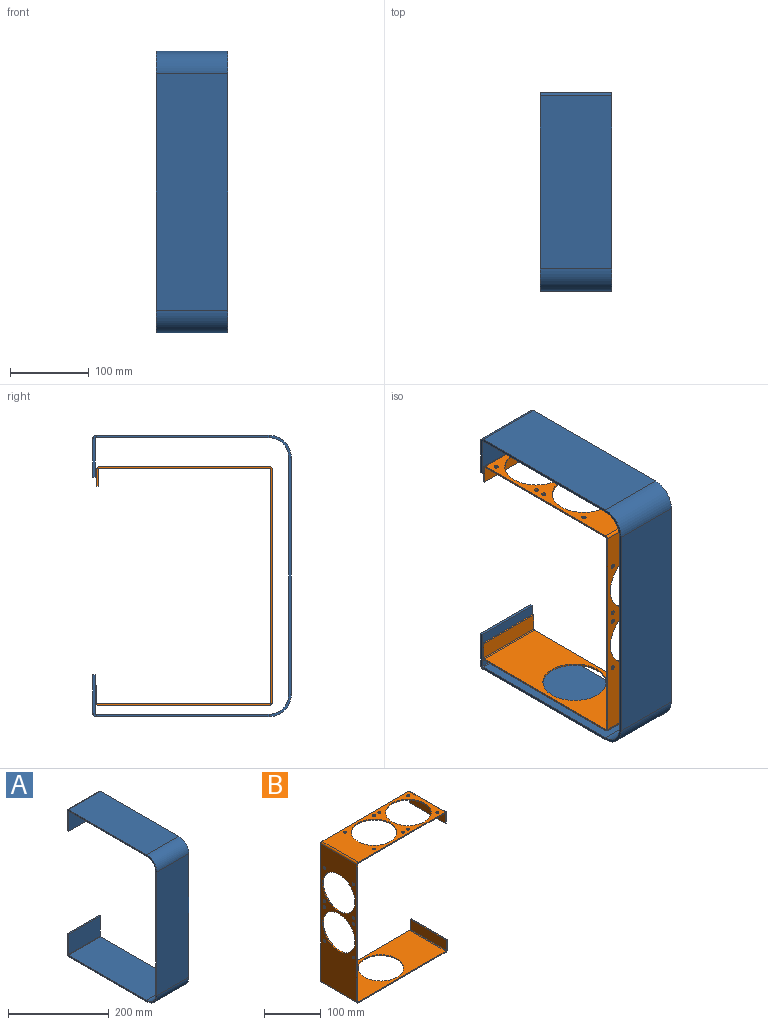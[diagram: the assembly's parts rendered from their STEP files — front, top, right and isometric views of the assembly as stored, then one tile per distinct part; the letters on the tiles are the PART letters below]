
ASSEMBLY  parts=2 mates=1
PART A: 38 faces, bbox 90x251.5x356.5 mm
  f0: plane 48.98x3.26mm, normal (-1,0,0), area 159.7mm2, adj f2,f3,f4,f18
  f1: plane 48.98x3.26mm, normal (1,0,0), area 159.7mm2, adj f2,f3,f4,f17
  f2: plane 90x3.26mm, normal (0,0,-1), area 293.4mm2, adj f0,f1,f3,f4
  f3: plane 90x48.98mm, normal (0,1,0), area 4408.6mm2, adj f0,f1,f2,f19
  f4: plane 90x48.98mm, normal (0,-1,0), area 4408.6mm2, adj f0,f1,f2,f20
  f5: plane 300x3.26mm, normal (-1,0,0), area 978mm2, adj f7,f8,f13,f34
  f6: plane 300x3.26mm, normal (1,0,0), area 978mm2, adj f7,f8,f14,f35
  f7: plane 300x90mm, normal (0,-1,0), area 27000mm2, adj f5,f6,f15,f36
  f8: plane 300x90mm, normal (0,1,0), area 27000mm2, adj f5,f6,f16,f37
  f9: plane 218.98x3.26mm, normal (-1,0,0), area 713.9mm2, adj f11,f12,f13,f18
  f10: plane 218.98x3.26mm, normal (1,0,0), area 713.9mm2, adj f11,f12,f14,f17
  f11: plane 218.98x90mm, normal (0,0,1), area 19708.6mm2, adj f9,f10,f15,f19
  f12: plane 218.98x90mm, normal (0,0,-1), area 19708.6mm2, adj f9,f10,f16,f20
  f13: plane 28.26x28.26mm, normal (-1,0,0), area 136.4mm2, adj f5,f9,f15,f16
  f14: plane 28.26x28.26mm, normal (1,0,0), area 136.4mm2, adj f6,f10,f15,f16
  f15: cylinder r=28.26mm len=90mm, axis (1,0,0), area 3995.2mm2, adj f7,f11,f13,f14
  f16: cylinder r=25mm len=90mm, axis (1,0,0), area 3534.3mm2, adj f8,f12,f13,f14
  f17: plane 4.28x4.28mm, normal (1,0,0), area 13.5mm2, adj f1,f10,f19,f20
  f18: plane 4.28x4.28mm, normal (-1,0,0), area 13.5mm2, adj f0,f9,f19,f20
  f19: cylinder r=4.28mm len=90mm, axis (1,0,0), area 604.5mm2, adj f3,f11,f17,f18
  f20: cylinder r=1.02mm len=90mm, axis (1,0,0), area 143.6mm2, adj f4,f12,f17,f18
  f21: plane 218.98x3.26mm, normal (-1,0,0), area 713.9mm2, adj f23,f24,f31,f34
  f22: plane 218.98x3.26mm, normal (1,0,0), area 713.9mm2, adj f23,f24,f30,f35
  f23: plane 218.98x90mm, normal (0,0,-1), area 19708.6mm2, adj f21,f22,f32,f36
  f24: plane 218.98x90mm, normal (0,0,1), area 19708.6mm2, adj f21,f22,f33,f37
  f25: plane 48.98x3.26mm, normal (-1,0,0), area 159.7mm2, adj f26,f28,f29,f31
  f26: plane 90x3.26mm, normal (0,0,1), area 293.4mm2, adj f25,f27,f28,f29
  f27: plane 48.98x3.26mm, normal (1,0,0), area 159.7mm2, adj f26,f28,f29,f30
  f28: plane 90x48.98mm, normal (0,1,0), area 4408.6mm2, adj f25,f26,f27,f32
  f29: plane 90x48.98mm, normal (0,-1,0), area 4408.6mm2, adj f25,f26,f27,f33
  f30: plane 4.28x4.28mm, normal (1,0,0), area 13.5mm2, adj f22,f27,f32,f33
  f31: plane 4.28x4.28mm, normal (-1,0,0), area 13.5mm2, adj f21,f25,f32,f33
  f32: cylinder r=4.28mm len=90mm, axis (1,0,0), area 604.5mm2, adj f23,f28,f30,f31
  f33: cylinder r=1.02mm len=90mm, axis (1,0,0), area 143.6mm2, adj f24,f29,f30,f31
  f34: plane 28.26x28.26mm, normal (-1,0,0), area 136.4mm2, adj f5,f21,f36,f37
  f35: plane 28.26x28.26mm, normal (1,0,0), area 136.4mm2, adj f6,f22,f36,f37
  f36: cylinder r=28.26mm len=90mm, axis (1,0,0), area 3995.2mm2, adj f7,f23,f34,f35
  f37: cylinder r=25mm len=90mm, axis (1,0,0), area 3534.3mm2, adj f8,f24,f34,f35
PART B: 59 faces, bbox 224.1x90x302.1 mm
  f0: plane 217.97x2.06mm, normal (0,-1,0), area 449mm2, adj f3,f4,f46,f55
  f1: plane 217.97x2.06mm, normal (0,1,0), area 449mm2, adj f3,f4,f47,f56
  f2: cylinder r=40mm len=80mm, axis (0,0,1), area 517.7mm2, adj f3,f4
  f3: plane 217.97x90mm, normal (0,0,-1), area 14590.6mm2, adj f0,f1,f2,f48,f57
  f4: plane 217.97x90mm, normal (0,0,1), area 14590.6mm2, adj f0,f1,f2,f49,f58
  f5: plane 295.91x2.06mm, normal (0,1,0), area 609.6mm2, adj f17,f18,f43,f47
  f6: cylinder r=2.75mm len=5.5mm, axis (-1,0,0), area 35.6mm2, adj f17,f18
  f7: cylinder r=2.75mm len=5.5mm, axis (-1,0,0), area 35.6mm2, adj f17,f18
  f8: cylinder r=2.75mm len=5.5mm, axis (-1,0,0), area 35.6mm2, adj f17,f18
  f9: cylinder r=2.75mm len=5.5mm, axis (-1,0,0), area 35.6mm2, adj f17,f18
  f10: cylinder r=2.75mm len=5.5mm, axis (-1,0,0), area 35.6mm2, adj f17,f18
  f11: cylinder r=2.75mm len=5.5mm, axis (-1,0,0), area 35.6mm2, adj f17,f18
  f12: cylinder r=2.75mm len=5.5mm, axis (-1,0,0), area 35.6mm2, adj f17,f18
  f13: cylinder r=2.75mm len=5.5mm, axis (-1,0,0), area 35.6mm2, adj f17,f18
  f14: cylinder r=40mm len=80mm, axis (-1,0,0), area 517.7mm2, adj f17,f18
  f15: cylinder r=40mm len=80mm, axis (-1,0,0), area 517.7mm2, adj f17,f18
  f16: plane 295.91x2.06mm, normal (0,-1,0), area 609.6mm2, adj f17,f18,f42,f46
  f17: plane 295.91x90mm, normal (-1,0,0), area 16388.6mm2, adj f5,f6,f7,f8,f9,f10,f11,f12
  f18: plane 295.91x90mm, normal (1,0,0), area 16388.6mm2, adj f5,f6,f7,f8,f9,f10,f11,f12
  f19: plane 215.91x2.06mm, normal (0,1,0), area 444.8mm2, adj f31,f32,f39,f43
  f20: cylinder r=2.75mm len=5.5mm, axis (0,0,1), area 35.6mm2, adj f31,f32
  f21: cylinder r=2.75mm len=5.5mm, axis (0,0,1), area 35.6mm2, adj f31,f32
  f22: cylinder r=2.75mm len=5.5mm, axis (0,0,1), area 35.6mm2, adj f31,f32
  f23: cylinder r=2.75mm len=5.5mm, axis (0,0,1), area 35.6mm2, adj f31,f32
  f24: cylinder r=2.75mm len=5.5mm, axis (0,0,1), area 35.6mm2, adj f31,f32
  f25: cylinder r=2.75mm len=5.5mm, axis (0,0,1), area 35.6mm2, adj f31,f32
  f26: cylinder r=2.75mm len=5.5mm, axis (0,0,1), area 35.6mm2, adj f31,f32
  f27: cylinder r=2.75mm len=5.5mm, axis (0,0,1), area 35.6mm2, adj f31,f32
  f28: cylinder r=40mm len=80mm, axis (0,0,1), area 517.7mm2, adj f31,f32
  f29: cylinder r=40mm len=80mm, axis (0,0,1), area 517.7mm2, adj f31,f32
  f30: plane 215.91x2.06mm, normal (0,-1,0), area 444.8mm2, adj f31,f32,f38,f42
  f31: plane 215.91x90mm, normal (0,0,1), area 9188.6mm2, adj f19,f20,f21,f22,f23,f24,f25,f26
  f32: plane 215.91x90mm, normal (0,0,-1), area 9188.6mm2, adj f19,f20,f21,f22,f23,f24,f25,f26
  f33: plane 90x2.06mm, normal (0,0,-1), area 185.4mm2, adj f34,f35,f36,f37
  f34: plane 21.92x2.06mm, normal (0,1,0), area 45.2mm2, adj f33,f36,f37,f39
  f35: plane 21.92x2.06mm, normal (0,-1,0), area 45.2mm2, adj f33,f36,f37,f38
  f36: plane 90x21.92mm, normal (1,0,0), area 1973.2mm2, adj f33,f34,f35,f40
  f37: plane 90x21.92mm, normal (-1,0,0), area 1973.2mm2, adj f33,f34,f35,f41
  f38: plane 3.08x3.08mm, normal (0,-1,0), area 6.6mm2, adj f30,f35,f40,f41
  f39: plane 3.08x3.08mm, normal (0,1,0), area 6.6mm2, adj f19,f34,f40,f41
  f40: cylinder r=3.08mm len=90mm, axis (0,-1,0), area 434.9mm2, adj f31,f36,f38,f39
  f41: cylinder r=1.02mm len=90mm, axis (0,-1,0), area 143.6mm2, adj f32,f37,f38,f39
  f42: plane 3.08x3.08mm, normal (0,-1,0), area 6.6mm2, adj f16,f30,f44,f45
  f43: plane 3.08x3.08mm, normal (0,1,0), area 6.6mm2, adj f5,f19,f44,f45
  f44: cylinder r=3.08mm len=90mm, axis (0,-1,0), area 434.9mm2, adj f17,f31,f42,f43
  f45: cylinder r=1.02mm len=90mm, axis (0,-1,0), area 143.6mm2, adj f18,f32,f42,f43
  f46: plane 3.08x3.08mm, normal (0,-1,0), area 6.6mm2, adj f0,f16,f48,f49
  f47: plane 3.08x3.08mm, normal (0,1,0), area 6.6mm2, adj f1,f5,f48,f49
  f48: cylinder r=3.08mm len=90mm, axis (0,-1,0), area 434.9mm2, adj f3,f17,f46,f47
  f49: cylinder r=1.02mm len=90mm, axis (0,-1,0), area 143.6mm2, adj f4,f18,f46,f47
  f50: plane 90x2.06mm, normal (0,0,1), area 185.4mm2, adj f51,f52,f53,f54
  f51: plane 21.92x2.06mm, normal (0,-1,0), area 45.2mm2, adj f50,f53,f54,f55
  f52: plane 21.92x2.06mm, normal (0,1,0), area 45.2mm2, adj f50,f53,f54,f56
  f53: plane 90x21.92mm, normal (1,0,0), area 1973.2mm2, adj f50,f51,f52,f57
  f54: plane 90x21.92mm, normal (-1,0,0), area 1973.2mm2, adj f50,f51,f52,f58
  f55: plane 3.08x3.08mm, normal (0,-1,0), area 6.6mm2, adj f0,f51,f57,f58
  f56: plane 3.08x3.08mm, normal (0,1,0), area 6.6mm2, adj f1,f52,f57,f58
  f57: cylinder r=3.08mm len=90mm, axis (0,-1,0), area 434.9mm2, adj f3,f53,f55,f56
  f58: cylinder r=1.02mm len=90mm, axis (0,-1,0), area 143.6mm2, adj f4,f54,f55,f56
PLACE A at identity
PLACE B rot(axis=(0,0,1),90deg) t=(28.11,-5.12,-163.53)mm
MATE slider B.f53 <-> A.f29  axis (0,1,0) through (45,110,-149.49)mm
